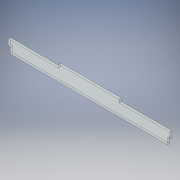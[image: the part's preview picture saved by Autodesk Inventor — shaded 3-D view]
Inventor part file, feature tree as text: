
AUTODESK INVENTOR PART (.ipt)
format: ipt  version: 2019 (Build 230136000, 136)  size: 146,432 bytes
history: native  units: mm
features: extrude x3, sketch x3, projected_geometry x2
ambient origin geometry x8: Origin, YZ Plane, XZ Plane, XY Plane, X Axis, Y Axis, Z Axis, Center Point
bodies: Solid1 (feature_tree)
feature tree (8):
  extrude  "Extrusion1"  Depth=267.0mm
  extrude  "Extrusion2"  Depth=10.0mm
  extrude  "Extrusion3"  Depth=100.0mm
  sketch  "Sketch1"  dims[d9=3.5mm d10=0.0mm d19=267.0mm]
  sketch  "Sketch2"  dims[d20=10.0mm d22=10.0mm]
  projected_geometry  "Projected Loop1"
  sketch  "Sketch3"  dims[d23=260.0mm d24=100.0mm d25=5.0mm d26=80.0mm d27=3.5mm d28=0.0mm d29=3.5mm d30=10.0mm d31=3.5mm d32=10.0mm d33=3.5mm d34=0.0mm]
  projected_geometry  "Projected Loop2"
